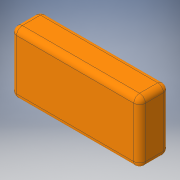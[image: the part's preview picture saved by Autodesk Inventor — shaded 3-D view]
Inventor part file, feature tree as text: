
AUTODESK INVENTOR PART (.ipt)
format: ipt  version: 2016 (Build 200138000, 138)  size: 129,024 bytes
history: native  units: in
note: dims shown in document units (in); Inventor stores cm internally (conversion verified against a paired STEP export)
features: extrude x1, fillet x1, sketch x1
ambient origin geometry x8: Origin, YZ Plane, XZ Plane, XY Plane, X Axis, Y Axis, Z Axis, Center Point
bodies: Solid1 (feature_tree)
feature tree (3):
  extrude  "Extrusion1"  Depth=1.34in
  fillet  "Fillet1"  Radius=0.64in
  sketch  "Sketch1"  dims[d0=2.782in d1=1.34in d2=0.64in d3=0.0in d4=0.125in]
